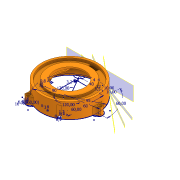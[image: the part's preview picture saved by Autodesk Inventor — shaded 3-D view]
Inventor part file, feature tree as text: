
AUTODESK INVENTOR PART (.ipt)
format: ipt  version: 2020.3 (Build 243373000, 373)  size: 384,000 bytes
history: native  units: mm
features: extrude x12, sketch x11, plane x4, revolve x1
ambient origin geometry x8: Origin, YZ Plane, XZ Plane, XY Plane, X Axis, Y Axis, Z Axis, Center Point
bodies: Body1 (feature_tree)
feature tree (28):
  sketch  "Sketch1"  dims[d0=95.0mm d1=120.0deg]
  plane  "Work Plane1"
  plane  "Work Plane2"
  plane  "Work Plane3"
  sketch  "Sketch2"  dims[d2=120.0deg d3=16.0mm]
  sketch  "Sketch3"  dims[d4=3.4mm d5=6.5mm]
  sketch  "Sketch4"  dims[d7=10.0mm d8=3.6mm]
  extrude  "Extrusion9"  TaperAngle=120.0deg  [1 undecoded]
  extrude  "Extrusion10"  Depth=16.0mm
  extrude  "Extrusion11"  Depth=6.5mm
  extrude  "Extrusion12"  Depth=10.0mm
  extrude  "Extrusion13"  Depth=1.2mm
  extrude  "Extrusion14"  Depth=9.8mm
  sketch  "Sketch5"  dims[d9=2.4mm d10=1.2mm]
  sketch  "Sketch6"  dims[d13=30.0mm d15=360.0deg d17=9.8mm]
  revolve  "Revolution1"  [1 undecoded]
  extrude  "Extrusion15"  Depth=2.0mm
  extrude  "Extrusion16"  Depth=6.1mm
  extrude  "Extrusion17"  Depth=6.1mm
  extrude  "Extrusion18"  Depth=2.5mm
  extrude  "Extrusion19"  Depth=2.5mm
  plane  "Work Plane4"
  extrude  "Extrusion20"  Depth=2.5mm
  sketch  "Sketch7"  dims[d18=12.0mm d19=2.0mm]
  sketch  "Sketch8"  dims[d20=6.0mm d21=2.0mm]
  sketch  "Sketch9"  dims[d23=60.0deg d24=6.1mm]
  sketch  "Sketch10"  dims[d25=8.0mm d26=6.1mm]
  sketch  "Sketch11"  dims[d27=60.0deg d28=1.745329mm d29=1.745329mm d46=5.5mm d47=5.5mm d48=5.5mm d56=40.0mm d57=60.0mm d58=3.2mm d59=1.3mm d60=1.0mm d61=1.0mm d62=1.3mm d64=3.0mm d65=8.0mm d66=6.0mm d74=90.0mm d75=26.0mm d76=0.0mm d77=3.0mm d78=0.0mm d79=10.0mm d80=0.0mm d81=10.0mm d82=0.0mm d83=4.2mm d84=0.0mm d85=8.4mm d86=0.0mm d87=70.0mm d88=85.0mm d89=3.75mm d90=4.0mm d91=8.5mm d92=50.5mm d93=2.0mm d94=2.0mm d95=4.0mm d96=90.0deg d97=23.5mm d98=0.0mm d99=12.5mm d100=0.0mm d101=6.5mm d102=6.0mm d103=6.0mm d104=3.0mm d105=0.0mm d106=7.25mm d107=0.0mm d108=3.490659mm d109=2.5mm d110=0.0mm d114=3.490659mm d115=4.0mm d116=4.0mm d117=90.0deg d118=5.0mm d119=2.5mm d120=12.0mm d121=0.0mm d72=0.5mm d73=0.872665mm d122=0.5mm d123=0.872665mm d124=0.5mm d125=0.872665mm]
note: 2 required parameter values undecoded (feature->parameter linkage not recoverable at this tier; creation-order binding heuristic only, values carry confidence <= 0.55)